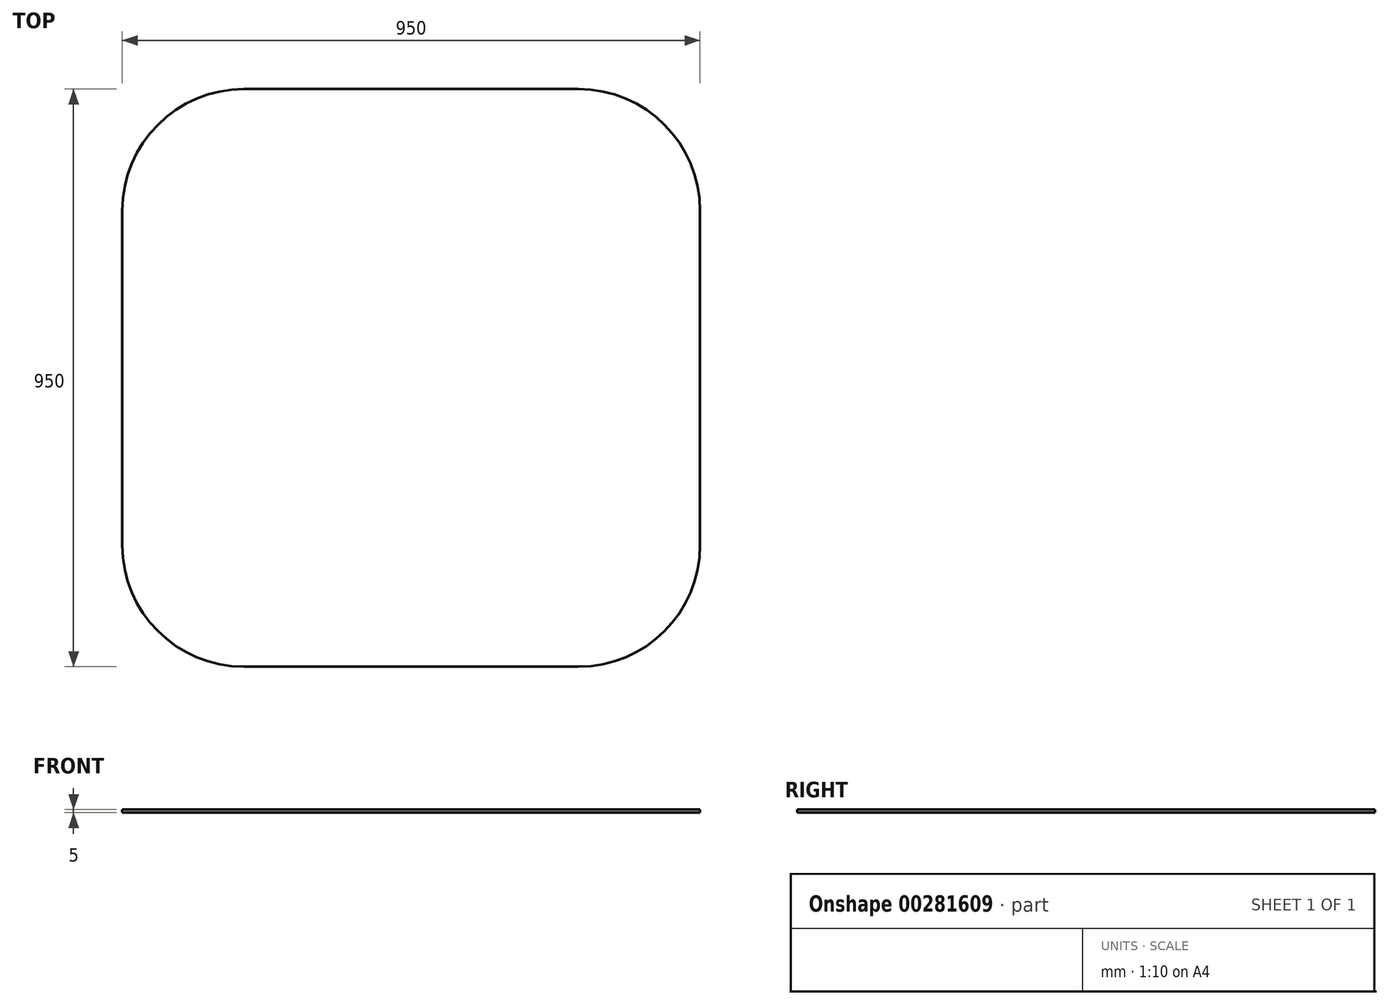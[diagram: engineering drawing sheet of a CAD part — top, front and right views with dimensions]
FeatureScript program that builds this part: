
annotation { "Feature Type Name" : "Feature", "Feature Type Description" : "" }
export const myFeature = defineFeature(function(context is Context, id is Id, definition is map)
    precondition{}
    {
        {
            var Q0;
            Q0=qCreatedBy(makeId("Top.planeOp"), FACE);
            var sketch = newSketch(context, id + "F0", { "sketchPlane" : qUnion([Q0])});
            skLineSegment(sketch, "E0.bottom", {"start": v(275, -475) * mm, "end": v(-275, -475) * mm});
            skLineSegment(sketch, "E0.top", {"start": v(275, 475) * mm, "end": v(-275, 475) * mm});
            skLineSegment(sketch, "E0.left", {"start": v(475, -275) * mm, "end": v(475, 275) * mm});
            skLineSegment(sketch, "E0.right", {"start": v(-475, -275) * mm, "end": v(-475, 275) * mm});
            skPoint(sketch, "E0.middle", {"position": v(0, 0) * mm});
            skPoint(sketch, "E1.visualSharp", {"position": v(-475, 475) * mm});
            skArc(sketch, "E1.filletArc", {"start": v(-275, 475) * mm, "mid": v(-416.42, 416.42) * mm, "end": v(-475, 275) * mm});
            skPoint(sketch, "E2.visualSharp", {"position": v(475, 475) * mm});
            skArc(sketch, "E2.filletArc", {"start": v(475, 275) * mm, "mid": v(416.42, 416.42) * mm, "end": v(275, 475) * mm});
            skPoint(sketch, "E3.visualSharp", {"position": v(475, -475) * mm});
            skArc(sketch, "E3.filletArc", {"start": v(275, -475) * mm, "mid": v(416.42, -416.42) * mm, "end": v(475, -275) * mm});
            skPoint(sketch, "E4.visualSharp", {"position": v(-475, -475) * mm});
            skArc(sketch, "E4.filletArc", {"start": v(-475, -275) * mm, "mid": v(-416.42, -416.42) * mm, "end": v(-275, -475) * mm});
            skSolve(sketch);
        }
        {
            var Q0;
            Q0 = qSketchRegion(id + "F0", true);
            extrude(context, id + "F1", {"entities" : qUnion([Q0]), "depth" : 5 * mm, "offsetDistance" : 25 * mm});
        }
    });
